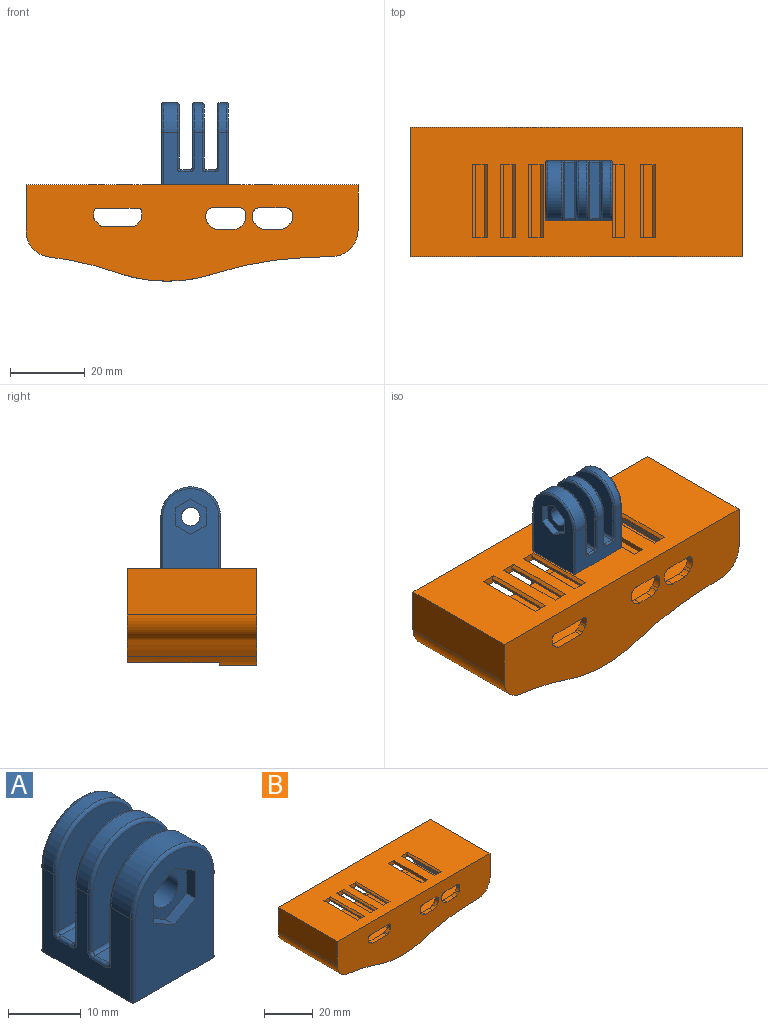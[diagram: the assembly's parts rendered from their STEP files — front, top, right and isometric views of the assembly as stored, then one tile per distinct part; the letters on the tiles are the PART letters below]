
ASSEMBLY  parts=2 mates=1
PART A: 58 faces, bbox 17.3x18x22.7 mm
  f0: plane 21.5x15mm, normal (0,-1,0), area 239.7mm2, adj f8,f48,f49,f50,f51,f52,f53,f54
  f1: plane 21.5x15mm, normal (0,1,0), area 278.7mm2, adj f8,f13,f45,f46,f47
  f2: plane 17x15mm, normal (0,-1,0), area 211.2mm2, adj f11,f17,f18,f20,f21
  f3: plane 17x15mm, normal (0,1,0), area 211.2mm2, adj f15,f26,f27,f29,f30
  f4: plane 17x15mm, normal (0,-1,0), area 211.2mm2, adj f13,f31,f32,f34,f35
  f5: plane 17x15mm, normal (0,1,0), area 211.2mm2, adj f11,f40,f41,f43,f44
  f6: plane 17x14mm, normal (-1,0,0), area 144.4mm2, adj f8,f12,f14,f16,f20,f23,f25,f28
  f7: plane 17x14mm, normal (1,0,0), area 144.4mm2, adj f8,f12,f14,f16,f17,f19,f22,f24
  f8: plane 18x16mm, normal (0,0,-1), area 287.8mm2, adj f0,f1,f6,f7,f45,f46,f48,f49
  f9: plane 15x2.5mm, normal (0,0,1), area 37.5mm2, adj f21,f22,f25,f26
  f10: plane 15x2.5mm, normal (0,0,1), area 37.5mm2, adj f35,f36,f39,f40
  f11: cylinder r=2.5mm len=5mm, axis (0,-1,0), area 50.3mm2, adj f2,f5
  f12: cylinder r=8mm len=16mm, axis (0,-1,0), area 55.3mm2, adj f6,f7,f18,f43
  f13: cylinder r=2.5mm len=5mm, axis (0,-1,0), area 47.1mm2, adj f1,f4
  f14: cylinder r=8mm len=16mm, axis (0,-1,0), area 50.3mm2, adj f6,f7,f32,f47
  f15: cylinder r=2.5mm len=5mm, axis (0,-1,0), area 47.1mm2, adj f3,f57
  f16: cylinder r=8mm len=16mm, axis (0,-1,0), area 95.5mm2, adj f6,f7,f29,f50
  f17: cylinder r=0.5mm len=9.5mm, axis (0,0,-1), area 7.5mm2, adj f2,f7,f18,f19
  f18: torus R=7.5mm, axis (0,-1,0), area 19.3mm2, adj f2,f12,f17,f20
  f19: torus R=1mm, axis (-1,0,0), area 0.8mm2, adj f7,f17,f21,f22
  f20: cylinder r=0.5mm len=9.5mm, axis (0,0,1), area 7.5mm2, adj f2,f6,f18,f23
  f21: cylinder r=0.5mm len=15mm, axis (-1,0,0), area 11.8mm2, adj f2,f9,f19,f23
  f22: cylinder r=0.5mm len=2.5mm, axis (0,-1,0), area 2mm2, adj f7,f9,f19,f24
  f23: torus R=1mm, axis (-1,0,0), area 0.8mm2, adj f6,f20,f21,f25
  f24: torus R=1mm, axis (-1,0,0), area 0.8mm2, adj f7,f22,f26,f27
  f25: cylinder r=0.5mm len=2.5mm, axis (0,1,0), area 2mm2, adj f6,f9,f23,f28
  f26: cylinder r=0.5mm len=15mm, axis (1,0,0), area 11.8mm2, adj f3,f9,f24,f28
  f27: cylinder r=0.5mm len=9.5mm, axis (0,0,1), area 7.5mm2, adj f3,f7,f24,f29
  f28: torus R=1mm, axis (-1,0,0), area 0.8mm2, adj f6,f25,f26,f30
  f29: torus R=7.5mm, axis (0,-1,0), area 19.3mm2, adj f3,f16,f27,f30
  f30: cylinder r=0.5mm len=9.5mm, axis (0,0,-1), area 7.5mm2, adj f3,f6,f28,f29
  f31: cylinder r=0.5mm len=9.5mm, axis (0,0,-1), area 7.5mm2, adj f4,f7,f32,f33
  f32: torus R=7.5mm, axis (0,-1,0), area 19.3mm2, adj f4,f14,f31,f34
  f33: torus R=1mm, axis (-1,0,0), area 0.8mm2, adj f7,f31,f35,f36
  f34: cylinder r=0.5mm len=9.5mm, axis (0,0,1), area 7.5mm2, adj f4,f6,f32,f37
  f35: cylinder r=0.5mm len=15mm, axis (-1,0,0), area 11.8mm2, adj f4,f10,f33,f37
  f36: cylinder r=0.5mm len=2.5mm, axis (0,-1,0), area 2mm2, adj f7,f10,f33,f38
  f37: torus R=1mm, axis (-1,0,0), area 0.8mm2, adj f6,f34,f35,f39
  f38: torus R=1mm, axis (-1,0,0), area 0.8mm2, adj f7,f36,f40,f41
  f39: cylinder r=0.5mm len=2.5mm, axis (0,1,0), area 2mm2, adj f6,f10,f37,f42
  f40: cylinder r=0.5mm len=15mm, axis (1,0,0), area 11.8mm2, adj f5,f10,f38,f42
  f41: cylinder r=0.5mm len=9.5mm, axis (0,0,1), area 7.5mm2, adj f5,f7,f38,f43
  f42: torus R=1mm, axis (-1,0,0), area 0.8mm2, adj f6,f39,f40,f44
  f43: torus R=7.5mm, axis (0,-1,0), area 19.3mm2, adj f5,f12,f41,f44
  f44: cylinder r=0.5mm len=9.5mm, axis (0,0,-1), area 7.5mm2, adj f5,f6,f42,f43
  f45: cylinder r=0.5mm len=14mm, axis (0,0,-1), area 11mm2, adj f1,f7,f8,f47
  f46: cylinder r=0.5mm len=14mm, axis (0,0,1), area 11mm2, adj f1,f6,f8,f47
  f47: torus R=7.5mm, axis (0,-1,0), area 19.3mm2, adj f1,f14,f45,f46
  f48: cylinder r=0.5mm len=14mm, axis (0,0,1), area 11mm2, adj f0,f7,f8,f50
  f49: cylinder r=0.5mm len=14mm, axis (0,0,-1), area 11mm2, adj f0,f6,f8,f50
  f50: torus R=7.5mm, axis (0,-1,0), area 19.3mm2, adj f0,f16,f48,f49
  f51: plane 4.11x2.38mm, normal (-0.5,0,0.87), area 8.6mm2, adj f0,f52,f56,f57
  f52: plane 4.75x1.8mm, normal (-1,0,0), area 8.6mm2, adj f0,f51,f53,f57
  f53: plane 4.11x2.38mm, normal (-0.5,0,-0.87), area 8.6mm2, adj f0,f52,f54,f57
  f54: plane 4.11x2.38mm, normal (0.5,0,-0.87), area 8.6mm2, adj f0,f53,f55,f57
  f55: plane 4.75x1.8mm, normal (1,0,0), area 8.6mm2, adj f0,f54,f56,f57
  f56: plane 4.11x2.38mm, normal (0.5,0,0.87), area 8.6mm2, adj f0,f51,f55,f57
  f57: plane 9.5x8.23mm, normal (0,-1,0), area 39mm2, adj f15,f51,f52,f53,f54,f55,f56
PART B: 121 faces, bbox 89x34.6x25.8 mm
  f0: plane 89x34.6mm, normal (0,0,1), area 2710.9mm2, adj f28,f29,f45,f52,f82,f84,f86,f88
  f1: plane 85x32.6mm, normal (0,0,-1), area 2263.8mm2, adj f2,f4,f47,f48,f52,f55,f56,f57
  f2: plane 75.5x14.93mm, normal (0,1,0), area 511.2mm2, adj f1,f5,f6,f7,f8,f9,f10,f11
  f3: plane 13.65x7.6mm, normal (0.07,0,1), area 104mm2, adj f46,f52,f69,f74
  f4: plane 62.5x16.3mm, normal (0,1,0), area 269.2mm2, adj f1,f46,f48,f49,f55,f58,f59,f60
  f5: plane 2x1.57mm, normal (1,0,0), area 3.1mm2, adj f2,f6,f44,f45
  f6: cylinder r=1mm len=2mm, axis (0,1,0), area 3.1mm2, adj f2,f5,f7,f45
  f7: plane 10.85x2mm, normal (0,0,-1), area 21.7mm2, adj f2,f6,f8,f45
  f8: cylinder r=1mm len=2mm, axis (0,1,0), area 3.1mm2, adj f2,f7,f9,f45
  f9: plane 2x1.57mm, normal (-1,0,0), area 3.1mm2, adj f2,f8,f10,f45
  f10: cylinder r=1mm len=2mm, axis (0,1,0), area 1.5mm2, adj f2,f9,f11,f45
  f11: plane 2x1.33mm, normal (-0.74,0,0.67), area 3.6mm2, adj f2,f10,f12,f45
  f12: cylinder r=1mm len=2mm, axis (0,1,0), area 1.7mm2, adj f2,f11,f13,f45
  f13: plane 8.42x2mm, normal (0,0,1), area 16.8mm2, adj f2,f12,f14,f45
  f14: cylinder r=1mm len=2mm, axis (0,1,0), area 1.7mm2, adj f2,f13,f15,f45
  f15: plane 2x1.33mm, normal (0.74,0,0.67), area 3.6mm2, adj f2,f14,f44,f45
  f16: plane 2x0.55mm, normal (1,0,0), area 1.1mm2, adj f2,f17,f41,f45
  f17: cylinder r=2mm len=2mm, axis (0,1,0), area 6.3mm2, adj f2,f16,f18,f45
  f18: plane 6.75x2mm, normal (0,0,-1), area 13.5mm2, adj f2,f17,f19,f45
  f19: cylinder r=2mm len=2mm, axis (0,1,0), area 6.3mm2, adj f2,f18,f20,f45
  f20: plane 2x0.55mm, normal (-1,0,0), area 1.1mm2, adj f2,f19,f21,f45
  f21: cylinder r=2.6mm len=2mm, axis (0,1,0), area 4mm2, adj f2,f20,f22,f45
  f22: plane 2x0.65mm, normal (-0.72,0,0.69), area 1.8mm2, adj f2,f21,f23,f45
  f23: cylinder r=2.6mm len=2mm, axis (0,1,0), area 4.2mm2, adj f2,f22,f24,f45
  f24: plane 4.3x2mm, normal (0,0,1), area 8.6mm2, adj f2,f23,f25,f45
  f25: cylinder r=2.6mm len=2mm, axis (0,1,0), area 4.2mm2, adj f2,f24,f26,f45
  f26: plane 2x0.65mm, normal (0.72,0,0.69), area 1.8mm2, adj f2,f25,f41,f45
  f27: plane 34.6x7.78mm, normal (0.04,0,-1), area 269.3mm2, adj f45,f52,f76,f78
  f28: plane 34.6x12.2mm, normal (1,0,0), area 422.1mm2, adj f0,f45,f52,f76
  f29: plane 34.6x12.34mm, normal (-1,0,0), area 427.1mm2, adj f0,f45,f52,f77
  f30: cylinder r=2.6mm len=27mm, axis (0,1,0), area 8mm2, adj f2,f31,f43,f45,f54,f57
  f31: plane 2x0.65mm, normal (-0.72,0,0.69), area 1.8mm2, adj f2,f30,f32,f45
  f32: cylinder r=2.6mm len=2mm, axis (0,1,0), area 4.2mm2, adj f2,f31,f33,f45
  f33: plane 4.3x2mm, normal (0,0,1), area 8.6mm2, adj f2,f32,f34,f45
  f34: cylinder r=2.6mm len=2mm, axis (0,1,0), area 4.2mm2, adj f2,f33,f35,f45
  f35: plane 2x0.65mm, normal (0.72,0,0.69), area 1.8mm2, adj f2,f34,f36,f45
  f36: cylinder r=2.6mm len=2mm, axis (0,1,0), area 4mm2, adj f2,f35,f37,f45
  f37: plane 2x0.55mm, normal (1,0,0), area 1.1mm2, adj f2,f36,f38,f45
  f38: cylinder r=2mm len=2mm, axis (0,1,0), area 6.3mm2, adj f2,f37,f39,f45
  f39: plane 6.75x2mm, normal (0,0,-1), area 13.5mm2, adj f2,f38,f40,f45
  f40: cylinder r=2mm len=27mm, axis (0,1,0), area 40.5mm2, adj f2,f39,f43,f45,f56,f57
  f41: cylinder r=2.6mm len=2mm, axis (0,1,0), area 4mm2, adj f2,f16,f26,f45
  f42: plane 10x0.27mm, normal (0,0,-1), area 2.7mm2, adj f45,f53,f80,f81
  f43: plane 27x0.55mm, normal (-1,0,0), area 14.8mm2, adj f30,f40,f45,f57
  f44: cylinder r=1mm len=2mm, axis (0,1,0), area 1.5mm2, adj f2,f5,f15,f45
  f45: plane 89x25.8mm, normal (0,-1,0), area 1753.5mm2, adj f0,f5,f6,f7,f8,f9,f10,f11
  f46: plane 34.6x32.6mm, normal (0,0,1), area 663.8mm2, adj f3,f4,f49,f50,f51,f52,f53,f58
  f47: plane 32.6x10.34mm, normal (1,0,0), area 337.2mm2, adj f1,f2,f52,f74
  f48: plane 32.6x10.2mm, normal (-1,0,0), area 332.5mm2, adj f1,f4,f52,f75
  f49: plane 32.6x27.3mm, normal (-0.04,0,1), area 890.8mm2, adj f4,f46,f52,f75
  f50: plane 24.6x6.89mm, normal (-1,0,0), area 169.6mm2, adj f46,f52,f53,f80
  f51: plane 24.6x6.81mm, normal (1,0,0), area 167.6mm2, adj f46,f52,f53,f81
  f52: plane 89x25.19mm, normal (0,1,0), area 473.5mm2, adj f0,f1,f3,f27,f28,f29,f46,f47
  f53: plane 14.6x7.5mm, normal (0,1,0), area 106.4mm2, adj f42,f46,f50,f51,f80,f81
  f54: plane 25x6.06mm, normal (0,0,-1), area 122.9mm2, adj f2,f30,f55,f57,f70,f73
  f55: plane 25x6.81mm, normal (1,0,0), area 146.2mm2, adj f1,f4,f54,f57,f72,f73
  f56: plane 25x4.84mm, normal (-1,0,0), area 120.9mm2, adj f1,f2,f40,f57
  f57: plane 6.81x5mm, normal (0,1,0), area 33.3mm2, adj f1,f30,f40,f43,f54,f55,f56
  f58: plane 25x1.2mm, normal (1,0,0), area 30mm2, adj f4,f46,f59,f69
  f59: plane 25x20.4mm, normal (0,0,-1), area 510mm2, adj f4,f58,f60,f69
  f60: plane 25x2.8mm, normal (1,0,0), area 70mm2, adj f4,f59,f61,f69
  f61: plane 34.6x25mm, normal (0,0,-1), area 684.5mm2, adj f4,f60,f62,f69,f71,f73
  f62: plane 19x2mm, normal (1,0,0), area 38mm2, adj f61,f63,f69,f73
  f63: plane 69x25mm, normal (0,0,1), area 1582.5mm2, adj f2,f62,f64,f69,f70,f73
  f64: plane 25x3.75mm, normal (1,0,0), area 93.7mm2, adj f2,f63,f65,f69
  f65: plane 25x9mm, normal (0,0,-1), area 225mm2, adj f2,f64,f66,f69
  f66: plane 25x4mm, normal (1,0,0), area 100mm2, adj f2,f65,f67,f69
  f67: plane 25x12.5mm, normal (0,0,1), area 312.5mm2, adj f2,f66,f68,f69
  f68: plane 25x12.38mm, normal (-1,0,0), area 309.4mm2, adj f2,f67,f69,f74
  f69: plane 65x13.75mm, normal (0,1,0), area 319.8mm2, adj f3,f46,f58,f59,f60,f61,f62,f63
  f70: plane 6x3.49mm, normal (-1,0,0), area 20.9mm2, adj f2,f54,f63,f73
  f71: plane 9.49x6mm, normal (1,0,0), area 56.9mm2, adj f4,f61,f72,f73
  f72: plane 6x3.5mm, normal (0,0,1), area 21mm2, adj f4,f55,f71,f73
  f73: plane 9.5x9.49mm, normal (0,1,0), area 40mm2, adj f54,f55,f61,f62,f63,f70,f71,f72
  f74: cylinder r=5mm len=32.6mm, axis (0,1,0), area 201.9mm2, adj f2,f3,f47,f52,f68,f69
  f75: cylinder r=5mm len=32.6mm, axis (0,1,0), area 249.4mm2, adj f4,f48,f49,f52
  f76: cylinder r=7mm len=34.6mm, axis (0,1,0), area 370.6mm2, adj f27,f28,f45,f52
  f77: cylinder r=7mm len=34.6mm, axis (0,1,0), area 350.5mm2, adj f29,f45,f52,f79
  f78: cylinder r=90mm len=34.6mm, axis (0,-1,0), area 852.5mm2, adj f27,f45,f52,f80
  f79: cylinder r=90mm len=34.6mm, axis (0,-1,0), area 655.9mm2, adj f45,f52,f77,f81
  f80: cylinder r=40mm len=34.6mm, axis (0,-1,0), area 263.4mm2, adj f42,f45,f50,f52,f53,f78
  f81: cylinder r=40mm len=34.6mm, axis (0,-1,0), area 279.9mm2, adj f42,f45,f51,f52,f53,f79
  f82: plane 3.9x2mm, normal (0,-1,0), area 6mm2, adj f0,f1,f83,f85,f102,f103,f112,f113
  f83: plane 19.6x0.6mm, normal (1,0,0), area 11.8mm2, adj f82,f84,f103,f113
  f84: plane 3.9x2mm, normal (0,1,0), area 6mm2, adj f0,f1,f83,f85,f102,f103,f112,f113
  f85: plane 19.6x0.6mm, normal (-1,0,0), area 11.8mm2, adj f82,f84,f102,f112
  f86: plane 3.9x2mm, normal (0,-1,0), area 5.7mm2, adj f0,f1,f87,f89,f104,f105,f114
  f87: plane 19.6x0.6mm, normal (1,0,0), area 11.8mm2, adj f86,f88,f105,f114
  f88: plane 3.9x2mm, normal (0,1,0), area 5.7mm2, adj f0,f1,f87,f89,f104,f105,f114
  f89: plane 19.6x1.3mm, normal (-1,0,0), area 25.5mm2, adj f0,f86,f88,f104
  f90: plane 3.9x2mm, normal (0,-1,0), area 6mm2, adj f0,f1,f91,f93,f106,f107,f115,f116
  f91: plane 19.6x0.6mm, normal (1,0,0), area 11.8mm2, adj f90,f92,f107,f116
  f92: plane 3.9x2mm, normal (0,1,0), area 6mm2, adj f0,f1,f91,f93,f106,f107,f115,f116
  f93: plane 19.6x0.6mm, normal (-1,0,0), area 11.8mm2, adj f90,f92,f106,f115
  f94: plane 19.6x0.6mm, normal (1,0,0), area 11.8mm2, adj f95,f97,f109,f118
  f95: plane 3.9x2mm, normal (0,1,0), area 6mm2, adj f0,f1,f94,f96,f108,f109,f117,f118
  f96: plane 19.6x0.6mm, normal (-1,0,0), area 11.8mm2, adj f95,f97,f108,f117
  f97: plane 3.9x2mm, normal (0,-1,0), area 6mm2, adj f0,f1,f94,f96,f108,f109,f117,f118
  f98: plane 3.9x2mm, normal (0,-1,0), area 6mm2, adj f0,f1,f99,f101,f110,f111,f119,f120
  f99: plane 19.6x0.6mm, normal (1,0,0), area 11.8mm2, adj f98,f100,f111,f120
  f100: plane 3.9x2mm, normal (0,1,0), area 6mm2, adj f0,f1,f99,f101,f110,f111,f119,f120
  f101: plane 19.6x0.6mm, normal (-1,0,0), area 11.8mm2, adj f98,f100,f110,f119
  f102: plane 19.6x0.7mm, normal (-0.71,0,-0.71), area 19.4mm2, adj f1,f82,f84,f85
  f103: plane 19.6x0.7mm, normal (0.71,0,-0.71), area 19.4mm2, adj f1,f82,f83,f84
  f104: plane 19.6x0.7mm, normal (-0.71,0,-0.71), area 19.4mm2, adj f1,f86,f88,f89
  f105: plane 19.6x0.7mm, normal (0.71,0,-0.71), area 19.4mm2, adj f1,f86,f87,f88
  f106: plane 19.6x0.7mm, normal (-0.71,0,-0.71), area 19.4mm2, adj f1,f90,f92,f93
  f107: plane 19.6x0.7mm, normal (0.71,0,-0.71), area 19.4mm2, adj f1,f90,f91,f92
  f108: plane 19.6x0.7mm, normal (-0.71,0,-0.71), area 19.4mm2, adj f1,f95,f96,f97
  f109: plane 19.6x0.7mm, normal (0.71,0,-0.71), area 19.4mm2, adj f1,f94,f95,f97
  f110: plane 19.6x0.7mm, normal (-0.71,0,-0.71), area 19.4mm2, adj f1,f98,f100,f101
  f111: plane 19.6x0.7mm, normal (0.71,0,-0.71), area 19.4mm2, adj f1,f98,f99,f100
  f112: plane 19.6x0.7mm, normal (-0.71,0,0.71), area 19.4mm2, adj f0,f82,f84,f85
  f113: plane 19.6x0.7mm, normal (0.71,0,0.71), area 19.4mm2, adj f0,f82,f83,f84
  f114: plane 19.6x0.7mm, normal (0.71,0,0.71), area 19.4mm2, adj f0,f86,f87,f88
  f115: plane 19.6x0.7mm, normal (-0.71,0,0.71), area 19.4mm2, adj f0,f90,f92,f93
  f116: plane 19.6x0.7mm, normal (0.71,0,0.71), area 19.4mm2, adj f0,f90,f91,f92
  f117: plane 19.6x0.7mm, normal (-0.71,0,0.71), area 19.4mm2, adj f0,f95,f96,f97
  f118: plane 19.6x0.7mm, normal (0.71,0,0.71), area 19.4mm2, adj f0,f94,f95,f97
  f119: plane 19.6x0.7mm, normal (-0.71,0,0.71), area 19.4mm2, adj f0,f98,f100,f101
  f120: plane 19.6x0.7mm, normal (0.71,0,0.71), area 19.4mm2, adj f0,f98,f99,f100
PLACE A rot(axis=(0,0,-1),90deg) t=(0.74,-0.61,11.8)mm
PLACE B at identity
MATE fastened A.f8 <-> B.f0  axis (0,0,-1) through (0.74,-0.61,11.8)mm
